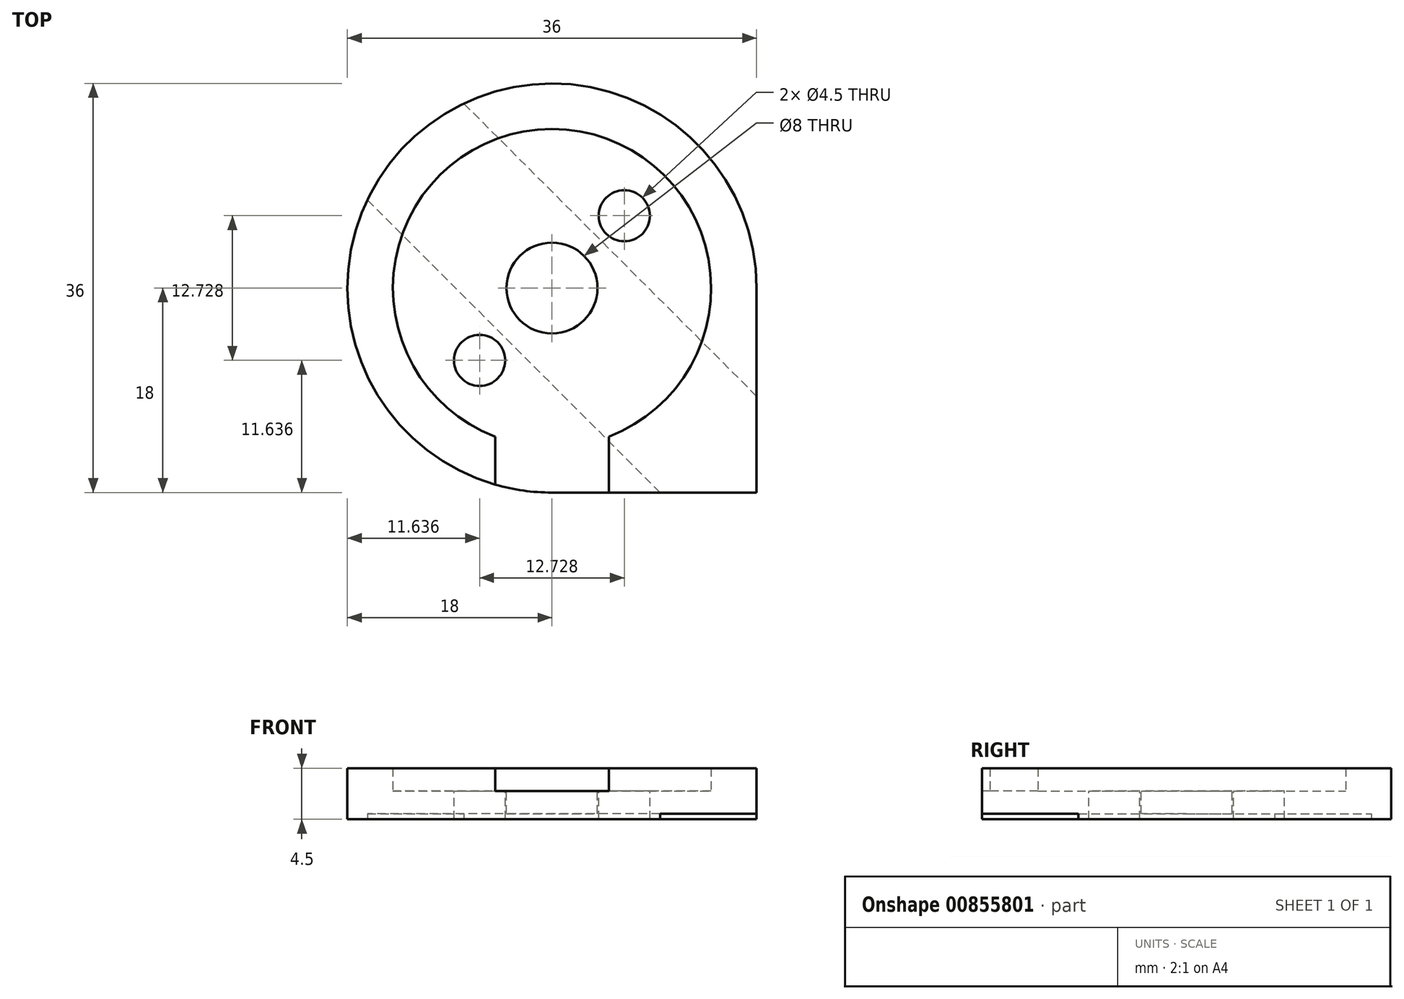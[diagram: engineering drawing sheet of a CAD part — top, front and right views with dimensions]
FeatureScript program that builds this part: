
annotation { "Feature Type Name" : "Feature", "Feature Type Description" : "" }
export const myFeature = defineFeature(function(context is Context, id is Id, definition is map)
    precondition{}
    {
        {
            var Q0;
            Q0=qCreatedBy(makeId("Top.planeOp"),FACE);
            var sketch = newSketch(context, id + "F0", { "sketchPlane" : qUnion([Q0])});
            skCircle(sketch, "E0", {"center": v(0, 0) * mm, "radius": 4 * mm});
            skLineSegment(sketch, "E1", {"start": v(0, 0) * mm, "end": v(0, 8) * mm});
            skCircle(sketch, "E2", {"center": v(6.36, 6.36) * mm, "radius": 2.25 * mm});
            skLineSegment(sketch, "E3", {"start": v(0, 0) * mm, "end": v(6.36, 6.36) * mm});
            skCircle(sketch, "E4.MirrorC", {"center": v(-6.36, -6.36) * mm, "radius": 2.25 * mm});
            skArc(sketch, "E5", {"start": v(0, 18) * mm, "mid": v(-12.73, 12.73) * mm, "end": v(-18, 0) * mm});
            skLineSegment(sketch, "E6", {"start": v(0, 0) * mm, "end": v(0, 0) * mm});
            skLineSegment(sketch, "E7", {"start": v(18, 0) * mm, "end": v(18, -18) * mm});
            skLineSegment(sketch, "E8", {"start": v(18, -18) * mm, "end": v(0, -18) * mm});
            skCircle(sketch, "E9", {"center": v(0, 0) * mm, "radius": 14 * mm});
            skLineSegment(sketch, "E10", {"start": v(0, 0) * mm, "end": v(18, 0) * mm});
            skLineSegment(sketch, "E11", {"start": v(-6.36, -6.36) * mm, "end": v(0, 0) * mm});
            skArc(sketch, "E12", {"start": v(-18, 0) * mm, "mid": v(-12.73, -12.73) * mm, "end": v(0, -18) * mm});
            skArc(sketch, "E13", {"start": v(18, 0) * mm, "mid": v(12.73, 12.73) * mm, "end": v(0, 18) * mm});
            skSolve(sketch);
        }
        {
            var Q0;
            {var subQ12=sQuery(id+"F0.wireOp",EDGE,"5gUyvu4n-H8Yu-rZ5o-7L1h-m2GLPaqCX34R");Q0=makeQuery(id+"F0.imprint","IMPRINT",FACE,{"disambiguationData":[TD([[makeQuery(id+"F0.imprint","IMPRINT",EDGE,{"derivedFrom":subQ12}),-1.0]])]});}
            var Q1;
            {var subQ10=sQuery(id+"F0.wireOp",EDGE,"E5");Q1=makeQuery(id+"F0.imprint","IMPRINT",FACE,{"disambiguationData":[TD([[makeQuery(id+"F0.imprint","IMPRINT",EDGE,{"derivedFrom":subQ10}),1.0]])]});}
            var Q2;
            {var subQ4=sQuery(id+"F0.wireOp",EDGE,"pYiCtXtq-HJty-5pja-FRCl-Y2SLxosvPTdB");Q2=makeQuery(id+"F0.imprint","IMPRINT",FACE,{"disambiguationData":[TD([[makeQuery(id+"F0.imprint","IMPRINT",EDGE,{"derivedFrom":subQ4}),-1.0]])]});}
            var Q3;
            {var subQ6=sQuery(id+"F0.wireOp",EDGE,"E7");Q3=makeQuery(id+"F0.imprint","IMPRINT",FACE,{"disambiguationData":[TD([[makeQuery(id+"F0.imprint","IMPRINT",EDGE,{"derivedFrom":subQ6}),-1.0]])]});}
            extrude(context, id + "F1", {"entities" : qUnion([Q0, Q1, Q2, Q3]), "depth" : 2 * mm, "offsetDistance" : 25 * mm});
        }
        {
            var Q0;
            Q0 = qSketchRegion(id + "F0", true);
            var Q1;
            {var subQ0=sQuery(id+"F0.wireOp",EDGE,"E10");var subQ5=sQuery(id+"F0.wireOp",EDGE,"E0");var subQ13=makeQuery(id+"F0.imprint","INTERSECT",VERTEX,{"derivedFrom":[subQ5,subQ0]});Q1=makeQuery(id+"F0.imprint","IMPRINT",FACE,{"disambiguationData":[TD([[makeQuery(id+"F0.imprint","IMPRINT",EDGE,{"disambiguationData":[TD([[subQ13,1.0]])],"derivedFrom":subQ5}),-1.0]])]});}
            var Q2;
            {var subQ0=sQuery(id+"F0.wireOp",EDGE,"9Jcqm4WY-S0i0-zeqv-JkX0-I8y0cwtzbrRk");var subQ8=sQuery(id+"F0.wireOp",EDGE,"E0");var subQ13=makeQuery(id+"F0.imprint","INTERSECT",VERTEX,{"derivedFrom":[subQ8,subQ0]});Q2=makeQuery(id+"F0.imprint","IMPRINT",FACE,{"disambiguationData":[TD([[makeQuery(id+"F0.imprint","IMPRINT",EDGE,{"disambiguationData":[TD([[subQ13,1.0]])],"derivedFrom":subQ8}),-1.0]])]});}
            var Q3;
            {var subQ0=sQuery(id+"F0.wireOp",EDGE,"9Jcqm4WY-S0i0-zeqv-JkX0-I8y0cwtzbrRk");var subQ11=sQuery(id+"F0.wireOp",EDGE,"E0");var subQ12=makeQuery(id+"F0.imprint","INTERSECT",VERTEX,{"derivedFrom":[subQ11,subQ0]});Q3=makeQuery(id+"F0.imprint","IMPRINT",FACE,{"disambiguationData":[TD([[makeQuery(id+"F0.imprint","IMPRINT",EDGE,{"disambiguationData":[TD([[subQ12,-1.0]])],"derivedFrom":subQ11}),-1.0]])]});}
            var Q4;
            {var subQ0=sQuery(id+"F0.wireOp",EDGE,"VnMWNyeu-xD8e-0Uzf-ypBL-w7x0ykIT27B9");var subQ8=sQuery(id+"F0.wireOp",EDGE,"E0");var subQ13=makeQuery(id+"F0.imprint","INTERSECT",VERTEX,{"derivedFrom":[subQ8,subQ0]});Q4=makeQuery(id+"F0.imprint","IMPRINT",FACE,{"disambiguationData":[TD([[makeQuery(id+"F0.imprint","IMPRINT",EDGE,{"disambiguationData":[TD([[subQ13,-1.0]])],"derivedFrom":subQ8}),-1.0]])]});}
            var Q5;
            {var subQ0=sQuery(id+"F0.wireOp",EDGE,"E10");var subQ1=sQuery(id+"F0.wireOp",EDGE,"E0");var subQ2=makeQuery(id+"F0.imprint","INTERSECT",VERTEX,{"derivedFrom":[subQ1,subQ0]});Q5=makeQuery(id+"F0.imprint","IMPRINT",FACE,{"disambiguationData":[TD([[makeQuery(id+"F0.imprint","IMPRINT",EDGE,{"disambiguationData":[TD([[subQ2,1.0]])],"derivedFrom":subQ1}),1.0]])]});}
            var Q6;
            {var subQ0=sQuery(id+"F0.wireOp",EDGE,"E3");var subQ1=sQuery(id+"F0.wireOp",EDGE,"E0");var subQ2=makeQuery(id+"F0.imprint","INTERSECT",VERTEX,{"derivedFrom":[subQ1,subQ0]});Q6=makeQuery(id+"F0.imprint","IMPRINT",FACE,{"disambiguationData":[TD([[makeQuery(id+"F0.imprint","IMPRINT",EDGE,{"disambiguationData":[TD([[subQ2,-1.0]])],"derivedFrom":subQ1}),1.0]])]});}
            var Q7;
            {var subQ0=sQuery(id+"F0.wireOp",EDGE,"E1");var subQ1=sQuery(id+"F0.wireOp",EDGE,"E0");var subQ2=makeQuery(id+"F0.imprint","INTERSECT",VERTEX,{"derivedFrom":[subQ1,subQ0]});Q7=makeQuery(id+"F0.imprint","IMPRINT",FACE,{"disambiguationData":[TD([[makeQuery(id+"F0.imprint","IMPRINT",EDGE,{"disambiguationData":[TD([[subQ2,-1.0]])],"derivedFrom":subQ1}),1.0]])]});}
            var Q8;
            {var subQ0=sQuery(id+"F0.wireOp",EDGE,"E3");var subQ1=sQuery(id+"F0.wireOp",EDGE,"E0");var subQ2=makeQuery(id+"F0.imprint","INTERSECT",VERTEX,{"derivedFrom":[subQ1,subQ0]});Q8=makeQuery(id+"F0.imprint","IMPRINT",FACE,{"disambiguationData":[TD([[makeQuery(id+"F0.imprint","IMPRINT",EDGE,{"disambiguationData":[TD([[subQ2,1.0]])],"derivedFrom":subQ1}),1.0]])]});}
            extrude(context, id + "F2", {"entities" : qUnion([Q0, Q1, Q2, Q3, Q4, Q5, Q6, Q7, Q8]), "operationType" : NewBodyOperationType.ADD, "oppositeDirection" : true, "depth" : 2.5 * mm, "offsetDistance" : 25 * mm});
        }
        {
            var Q0;
            {var subQ0=sQuery(id+"F0.wireOp",EDGE,"E10");var subQ1=sQuery(id+"F0.wireOp",EDGE,"E0");var subQ2=makeQuery(id+"F0.imprint","INTERSECT",VERTEX,{"derivedFrom":[subQ1,subQ0]});Q0=makeQuery(id+"F0.imprint","IMPRINT",FACE,{"disambiguationData":[TD([[makeQuery(id+"F0.imprint","IMPRINT",EDGE,{"disambiguationData":[TD([[subQ2,1.0]])],"derivedFrom":subQ1}),1.0]])]});}
            var Q1;
            {var subQ0=sQuery(id+"F0.wireOp",EDGE,"E3");var subQ1=sQuery(id+"F0.wireOp",EDGE,"E0");var subQ2=makeQuery(id+"F0.imprint","INTERSECT",VERTEX,{"derivedFrom":[subQ1,subQ0]});Q1=makeQuery(id+"F0.imprint","IMPRINT",FACE,{"disambiguationData":[TD([[makeQuery(id+"F0.imprint","IMPRINT",EDGE,{"disambiguationData":[TD([[subQ2,1.0]])],"derivedFrom":subQ1}),1.0]])]});}
            var Q2;
            {var subQ0=sQuery(id+"F0.wireOp",EDGE,"E3");var subQ1=sQuery(id+"F0.wireOp",EDGE,"E0");var subQ2=makeQuery(id+"F0.imprint","INTERSECT",VERTEX,{"derivedFrom":[subQ1,subQ0]});Q2=makeQuery(id+"F0.imprint","IMPRINT",FACE,{"disambiguationData":[TD([[makeQuery(id+"F0.imprint","IMPRINT",EDGE,{"disambiguationData":[TD([[subQ2,-1.0]])],"derivedFrom":subQ1}),1.0]])]});}
            var Q3;
            {var subQ0=sQuery(id+"F0.wireOp",EDGE,"E1");var subQ1=sQuery(id+"F0.wireOp",EDGE,"E0");var subQ2=makeQuery(id+"F0.imprint","INTERSECT",VERTEX,{"derivedFrom":[subQ1,subQ0]});Q3=makeQuery(id+"F0.imprint","IMPRINT",FACE,{"disambiguationData":[TD([[makeQuery(id+"F0.imprint","IMPRINT",EDGE,{"disambiguationData":[TD([[subQ2,-1.0]])],"derivedFrom":subQ1}),1.0]])]});}
            extrude(context, id + "F3", {"entities" : qUnion([Q0, Q1, Q2, Q3]), "operationType" : NewBodyOperationType.REMOVE, "oppositeDirection" : true, "depth" : 3 * mm, "offsetDistance" : 25 * mm});
        }
        {
            var Q0;
            Q0=makeQuery(id+"F2.opExtrude","CAP_FACE",FACE,{"disambiguationData":[OSD([sQuery(id+"F0.wireOp",EDGE,"E2"),sQuery(id+"F0.wireOp",EDGE,"E4.MirrorC"),sQuery(id+"F0.wireOp",EDGE,"E5"),sQuery(id+"F0.wireOp",EDGE,"5gUyvu4n-H8Yu-rZ5o-7L1h-m2GLPaqCX34R"),sQuery(id+"F0.wireOp",EDGE,"1Qr6Kwjt-veDL-C7E2-Esiv-kxE1Q1Ce19U3"),sQuery(id+"F0.wireOp",EDGE,"pYiCtXtq-HJty-5pja-FRCl-Y2SLxosvPTdB"),sQuery(id+"F0.wireOp",EDGE,"jzTP4OU7-n7uz-U0up-Kohm-FM5JfBalmunU"),sQuery(id+"F0.wireOp",EDGE,"E7"),sQuery(id+"F0.wireOp",EDGE,"E8")])],"isStart":false});
            var sketch = newSketch(context, id + "F4", { "sketchPlane" : qUnion([Q0])});
            skLineSegment(sketch, "E14", {"start": v(0, 0) * mm, "end": v(-4.24, 4.24) * mm});
            skLineSegment(sketch, "E15", {"start": v(0, 0) * mm, "end": v(4.24, -4.24) * mm});
            skLineSegment(sketch, "E16", {"start": v(4.24, -4.24) * mm, "end": v(18, 9.51) * mm});
            skLineSegment(sketch, "E17", {"start": v(-4.24, 4.24) * mm, "end": v(9.51, 18) * mm});
            skLineSegment(sketch, "E18", {"start": v(-4.24, 4.24) * mm, "end": v(-16.97, -8.49) * mm});
            skLineSegment(sketch, "E19", {"start": v(4.24, -4.24) * mm, "end": v(-8.49, -16.97) * mm});
            skLineSegment(sketch, "E20", {"start": v(-16.97, -8.49) * mm, "end": v(-8.49, -16.97) * mm});
            skLineSegment(sketch, "E21", {"start": v(18, 0) * mm, "end": v(0, 0) * mm});
            skSolve(sketch);
        }
        {
            var Q0;
            Q0 = qSketchRegion(id + "F4", true);
            var Q1;
            {var subQ2=sQuery(id+"F4.wireOp",EDGE,"E14");Q1=makeQuery(id+"F4.imprint","IMPRINT",FACE,{"disambiguationData":[TD([[makeQuery(id+"F4.imprint","IMPRINT",EDGE,{"derivedFrom":subQ2}),-1.0]])]});}
            var Q2;
            {var subQ11=sQuery(id+"F4.wireOp",EDGE,"E17");Q2=makeQuery(id+"F4.imprint","IMPRINT",FACE,{"disambiguationData":[TD([[makeQuery(id+"F4.imprint","IMPRINT",EDGE,{"derivedFrom":subQ11}),-1.0]])]});}
            extrude(context, id + "F5", {"entities" : qUnion([Q0, Q1, Q2]), "operationType" : NewBodyOperationType.REMOVE, "oppositeDirection" : true, "depth" : 0.5 * mm, "offsetDistance" : 25 * mm});
        }
        {
            var Q0;
            Q0=makeQuery(id+"F1.opExtrude","CAP_FACE",FACE,{"disambiguationData":[OSD([sQuery(id+"F0.wireOp",EDGE,"E5"),sQuery(id+"F0.wireOp",EDGE,"E7"),sQuery(id+"F0.wireOp",EDGE,"E8"),sQuery(id+"F0.wireOp",EDGE,"E9"),sQuery(id+"F0.wireOp",EDGE,"E12"),sQuery(id+"F0.wireOp",EDGE,"E13")])],"isStart":false});
            var sketch = newSketch(context, id + "F6", { "sketchPlane" : qUnion([Q0])});
            skLineSegment(sketch, "E22", {"start": v(0, 0) * mm, "end": v(0, -18) * mm});
            skLineSegment(sketch, "E23.bottom", {"start": v(5, -9) * mm, "end": v(-5, -9) * mm});
            skLineSegment(sketch, "E23.top", {"start": v(5, -19) * mm, "end": v(-5, -19) * mm});
            skLineSegment(sketch, "E23.left", {"start": v(5, -9) * mm, "end": v(5, -19) * mm});
            skLineSegment(sketch, "E23.right", {"start": v(-5, -9) * mm, "end": v(-5, -19) * mm});
            skPoint(sketch, "E23.middle", {"position": v(0, -14) * mm});
            skSolve(sketch);
        }
        {
            var Q0;
            {var subQ0=sQuery(id+"F6.wireOp",EDGE,"E23.bottom");var subQ1=sQuery(id+"F6.wireOp",EDGE,"E22");var subQ2=makeQuery(id+"F6.imprint","INTERSECT",VERTEX,{"derivedFrom":[subQ1,subQ0]});Q0=makeQuery(id+"F6.imprint","IMPRINT",FACE,{"disambiguationData":[TD([[makeQuery(id+"F6.imprint","IMPRINT",EDGE,{"disambiguationData":[TD([[subQ2,-1.0]])],"derivedFrom":subQ1}),1.0]])]});}
            var Q1;
            {var subQ0=sQuery(id+"F6.wireOp",EDGE,"E23.bottom");var subQ1=sQuery(id+"F6.wireOp",EDGE,"E22");var subQ2=makeQuery(id+"F6.imprint","INTERSECT",VERTEX,{"derivedFrom":[subQ1,subQ0]});Q1=makeQuery(id+"F6.imprint","IMPRINT",FACE,{"disambiguationData":[TD([[makeQuery(id+"F6.imprint","IMPRINT",EDGE,{"disambiguationData":[TD([[subQ2,-1.0]])],"derivedFrom":subQ1}),-1.0]])]});}
            var Q2;
            {var subQ1=sQuery(id+"F6.wireOp",EDGE,"E23.top");Q2=makeQuery(id+"F6.imprint","IMPRINT",FACE,{"disambiguationData":[TD([[makeQuery(id+"F6.imprint","IMPRINT",EDGE,{"derivedFrom":subQ1}),-1.0]])]});}
            var Q3;
            {var subQ1=makeQuery(id+"F1.opExtrude","CAP_EDGE",EDGE,{"disambiguationData":[OSD([sQuery(id+"F0.wireOp",EDGE,"E8")])],"isStart":false});var subQ5=sQuery(id+"F6.wireOp",EDGE,"E23.left");var subQ6=makeQuery(id+"F6.imprint","INTERSECT",VERTEX,{"derivedFrom":[subQ1,subQ5]});Q3=makeQuery(id+"F6.imprint","IMPRINT",FACE,{"disambiguationData":[TD([[makeQuery(id+"F6.imprint","IMPRINT",EDGE,{"disambiguationData":[TD([[subQ6,1.0]])],"derivedFrom":subQ5}),-1.0]])]});}
            var Q4;
            {var subQ0=sQuery(id+"F6.wireOp",EDGE,"E22");var subQ3=makeQuery(id+"F1.opExtrude","CAP_EDGE",EDGE,{"disambiguationData":[OSD([sQuery(id+"F0.wireOp",EDGE,"E9")])],"isStart":false});var subQ4=makeQuery(id+"F6.imprint","INTERSECT",VERTEX,{"derivedFrom":[subQ3,subQ0]});Q4=makeQuery(id+"F6.imprint","IMPRINT",FACE,{"disambiguationData":[TD([[makeQuery(id+"F6.imprint","IMPRINT",EDGE,{"disambiguationData":[TD([[subQ4,1.0]])],"derivedFrom":subQ3}),-1.0]])]});}
            extrude(context, id + "F7", {"entities" : qUnion([Q0, Q1, Q2, Q3, Q4]), "operationType" : NewBodyOperationType.REMOVE, "oppositeDirection" : true, "depth" : 2 * mm, "offsetDistance" : 25 * mm});
        }
    });
